# Revit family: Table-Teknion- CWTQF_C+D_Square_Table_Flat_Edge-R2020
name_source: partatom
category: Furniture
units: mm (PartAtom-declared; Revit-internal decimal feet)

## family parameters
Always vertical = Yes
Cut with Voids When Loaded = No
OmniClass Number = 23.40.20.00
OmniClass Title = General Furniture and Specialties
Room Calculation Point = No
Shared = Yes
Work Plane-Based = No

## types (4) — shared parameters
Assembly Code = E2020200
Manufacturer = Teknion
Manufacturer Fax = 416.661.4586
Part Number = CWTQF
Product Documentation Link = https://www.teknion.com
Product Line = C+D
Product Page URL = https://www.teknion.com
Series = Custom Wood
Sustainability Data = https://www.teknion.com
URL = www.teknion.com
Unit Weight URL = http://www.teknion.com
Warranty = http://www.teknion.com
zero-valued in all types: Default Elevation

## per-type parameters (varying)
| type | Central Plinth Finishes | Description | Model | Open Leg Base | Round Corner | Square Corner | Standard Base with Central Plinth |
| Round Corner, Open Leg Base | Veneer - Teknion - VJ - Bistre | Custom Wood C+D Square Table, Flat Edge, Round Corner, Open Leg Base | CWTQFRB | Yes | Yes | No | No |
| Round Corner, Standard Base with Central Plinth | Veneer-Teknion-UN-Natural_Veneer_V2-Walnut_On_Cherry | Custom Wood C+D Square Table, Flat Edge, Round Corner, Standard Base with Central Plinth | CWTQFRP | No | Yes | No | Yes |
| Square Corner, Open Leg Base | Veneer-Teknion-LQ-Natural_Veneer_V3-Poppy_Seed_Flat_Cut | Custom Wood C+D Square Table, Flat Edge, Square Corner, Open Leg Base | CWTQFSB | Yes | No | Yes | No |
| Square Corner, Standard Base with Central Plinth | Veneer-Teknion-LV-Natural_Veneer_V3-Natural_Pecan_Flat_Cut | Custom Wood C+D Square Table, Flat Edge, Square Corner, Standard Base with Central Plinth | CWTQFSP | No | No | Yes | Yes |

## geometry (parser evidence)
native form markers: Sweep x3
no freeform markers — native parametric forms only
